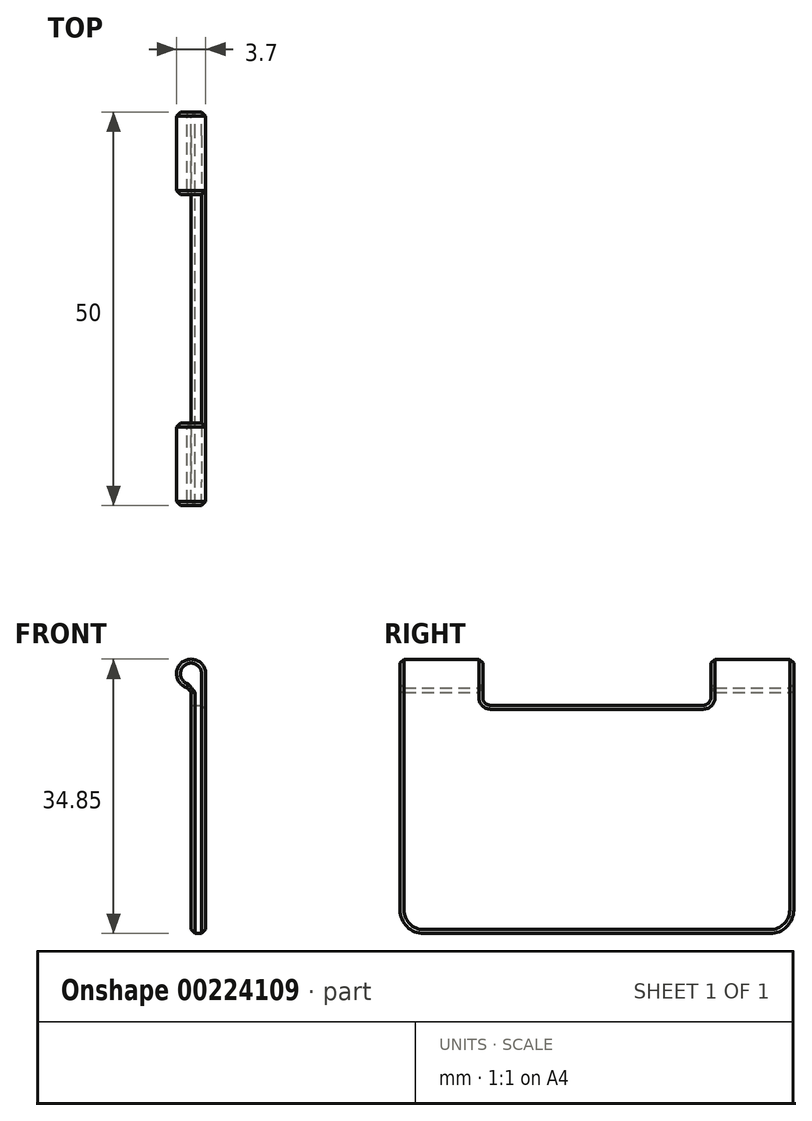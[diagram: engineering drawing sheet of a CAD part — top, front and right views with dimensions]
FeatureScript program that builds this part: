
annotation { "Feature Type Name" : "Feature", "Feature Type Description" : "" }
export const myFeature = defineFeature(function(context is Context, id is Id, definition is map)
    precondition{}
    {
        {
            var Q0;
            Q0=qCreatedBy(makeId("Front.planeOp"),FACE);
            var sketch = newSketch(context, id + "F0", { "sketchPlane" : qUnion([Q0])});
            skLineSegment(sketch, "E0.top", {"start": v(-0.1, -0.84) * mm, "end": v(1.74, -0.84) * mm});
            skLineSegment(sketch, "E0.left", {"start": v(-0.1, 30.3) * mm, "end": v(-0.1, -0.84) * mm});
            skLineSegment(sketch, "E0.right", {"start": v(1.74, 32.16) * mm, "end": v(1.74, -0.84) * mm});
            skArc(sketch, "E1", {"start": v(1.74, 32.16) * mm, "mid": v(-1.41, 33.46) * mm, "end": v(-0.1, 30.3) * mm});
            skPoint(sketch, "E2.visualSharp", {"position": v(-0.1, -0.84) * mm});
            skPoint(sketch, "E3.visualSharp", {"position": v(1.74, -0.84) * mm});
            skSolve(sketch);
        }
        {
            var Q0;
            Q0=makeQuery(id+"F0.imprint","IMPRINT",FACE,{"disambiguationData":[TD([[makeQuery(id+"F0.imprint","IMPRINT",EDGE,{"derivedFrom":sQuery(id+"F0.wireOp",EDGE,"E0.top")}),1.0]])]});
            extrude(context, id + "F1", {"entities" : qUnion([Q0]), "depth" : 50 * mm});
        }
        {
            var Q0;
            Q0=makeQuery(id+"F1.opExtrude","CAP_EDGE",EDGE,{"disambiguationData":[OSD([sQuery(id+"F0.wireOp",EDGE,"E0.top")])],"isStart":false});
            var Q1;
            Q1=makeQuery(id+"F1.opExtrude","CAP_EDGE",EDGE,{"disambiguationData":[OSD([sQuery(id+"F0.wireOp",EDGE,"E0.top")])],"isStart":true});
            fillet(context, id + "F2", {"entities" : qUnion([Q0, Q1]), "radius" : 3 * mm, "tangentPropagation" : true, "allowEdgeOverflow" : false});
        }
        {
            var Q0;
            Q0=makeQuery(id+"F1.opExtrude","SWEPT_FACE",FACE,{"disambiguationData":[OSD([sQuery(id+"F0.wireOp",EDGE,"E0.right")])]});
            var Q1;
            Q1=makeQuery(id+"F1.opExtrude","SWEPT_FACE",FACE,{"disambiguationData":[OSD([sQuery(id+"F0.wireOp",EDGE,"E0.left")])]});
            chamfer(context, id + "F3", {"entities" : qUnion([Q0, Q1]), "width" : .5 * mm, "tangentPropagation" : true});
        }
        {
            var Q0;
            Q0=makeQuery(id+"F1.opExtrude","SWEPT_FACE",FACE,{"disambiguationData":[OSD([sQuery(id+"F0.wireOp",EDGE,"E0.right")])]});
            var sketch = newSketch(context, id + "F4", { "sketchPlane" : qUnion([Q0])});
            skLineSegment(sketch, "E4.bottom", {"start": v(-11.5, 28.16) * mm, "end": v(-38.5, 28.16) * mm});
            skLineSegment(sketch, "E4.top", {"start": v(-10.5, 35.22) * mm, "end": v(-39.5, 35.22) * mm});
            skLineSegment(sketch, "E4.left", {"start": v(-10.5, 29.16) * mm, "end": v(-10.5, 35.22) * mm});
            skLineSegment(sketch, "E4.right", {"start": v(-39.5, 29.16) * mm, "end": v(-39.5, 35.22) * mm});
            skPoint(sketch, "E5.visualSharp", {"position": v(-39.5, 28.16) * mm});
            skArc(sketch, "E5.filletArc", {"start": v(-39.5, 29.16) * mm, "mid": v(-39.2, 28.45) * mm, "end": v(-38.5, 28.16) * mm});
            skPoint(sketch, "E6.visualSharp", {"position": v(-10.5, 28.16) * mm});
            skArc(sketch, "E6.filletArc", {"start": v(-11.5, 28.16) * mm, "mid": v(-10.8, 28.45) * mm, "end": v(-10.5, 29.16) * mm});
            skSolve(sketch);
        }
        {
            var Q0;
            {var subQ0=sQuery(id+"F4.wireOp",EDGE,"E4.top");Q0=makeQuery(id+"F4.imprint","IMPRINT",FACE,{"disambiguationData":[TD([[makeQuery(id+"F4.imprint","IMPRINT",EDGE,{"derivedFrom":subQ0}),1.0]])]});}
            var Q1;
            {var subQ0=sQuery(id+"F4.wireOp",EDGE,"E4.bottom");Q1=makeQuery(id+"F4.imprint","IMPRINT",FACE,{"disambiguationData":[TD([[makeQuery(id+"F4.imprint","IMPRINT",EDGE,{"derivedFrom":subQ0}),-1.0]])]});}
            extrude(context, id + "F5", {"entities" : qUnion([Q0, Q1]), "operationType" : NewBodyOperationType.REMOVE, "oppositeDirection" : true, "depth" : 25 * mm, "offsetDistance" : 25 * mm});
        }
        {
            var Q0;
            {var subQ0=sQuery(id+"F0.wireOp",EDGE,"E1");var subQ1=sQuery(id+"F0.wireOp",EDGE,"E0.left");Q0=makeQuery(id+"F5.boolean.opBoolean","INTERSECT",EDGE,{"derivedFrom":[makeQuery(id+"F3.opChamfer","BLEND_FACE",FACE,{"disambiguationData":[OSD([subQ1,subQ0]),TDD([makeQuery(id+"F1.opExtrude","SWEPT_EDGE",EDGE,{"disambiguationData":[OSD([subQ1,subQ0])]})])]}),makeQuery(id+"F5.opExtrude","SWEPT_FACE",FACE,{"disambiguationData":[OSD([sQuery(id+"F4.wireOp",EDGE,"E4.left")])]})]});}
            var Q1;
            Q1=makeQuery(id+"F5.boolean.opBoolean","INTERSECT",EDGE,{"derivedFrom":[makeQuery(id+"F1.opExtrude","SWEPT_FACE",FACE,{"disambiguationData":[OSD([sQuery(id+"F0.wireOp",EDGE,"E1")])]}),makeQuery(id+"F5.opExtrude","SWEPT_FACE",FACE,{"disambiguationData":[OSD([sQuery(id+"F4.wireOp",EDGE,"E4.left")])]})]});
            var Q2;
            {var subQ0=sQuery(id+"F0.wireOp",EDGE,"E1");var subQ1=sQuery(id+"F0.wireOp",EDGE,"E0.left");Q2=makeQuery(id+"F5.boolean.opBoolean","INTERSECT",EDGE,{"derivedFrom":[makeQuery(id+"F3.opChamfer","BLEND_FACE",FACE,{"disambiguationData":[OSD([subQ1,subQ0]),TDD([makeQuery(id+"F1.opExtrude","SWEPT_EDGE",EDGE,{"disambiguationData":[OSD([subQ1,subQ0])]})])]}),makeQuery(id+"F5.opExtrude","SWEPT_FACE",FACE,{"disambiguationData":[OSD([sQuery(id+"F4.wireOp",EDGE,"E4.right")])]})]});}
            var Q3;
            Q3=makeQuery(id+"F5.boolean.opBoolean","INTERSECT",EDGE,{"derivedFrom":[makeQuery(id+"F1.opExtrude","SWEPT_FACE",FACE,{"disambiguationData":[OSD([sQuery(id+"F0.wireOp",EDGE,"E1")])]}),makeQuery(id+"F5.opExtrude","SWEPT_FACE",FACE,{"disambiguationData":[OSD([sQuery(id+"F4.wireOp",EDGE,"E4.right")])]})]});
            chamfer(context, id + "F6", {"entities" : qUnion([Q0, Q1, Q2, Q3]), "width" : 0.5 * mm, "tangentPropagation" : true});
        }
    });
